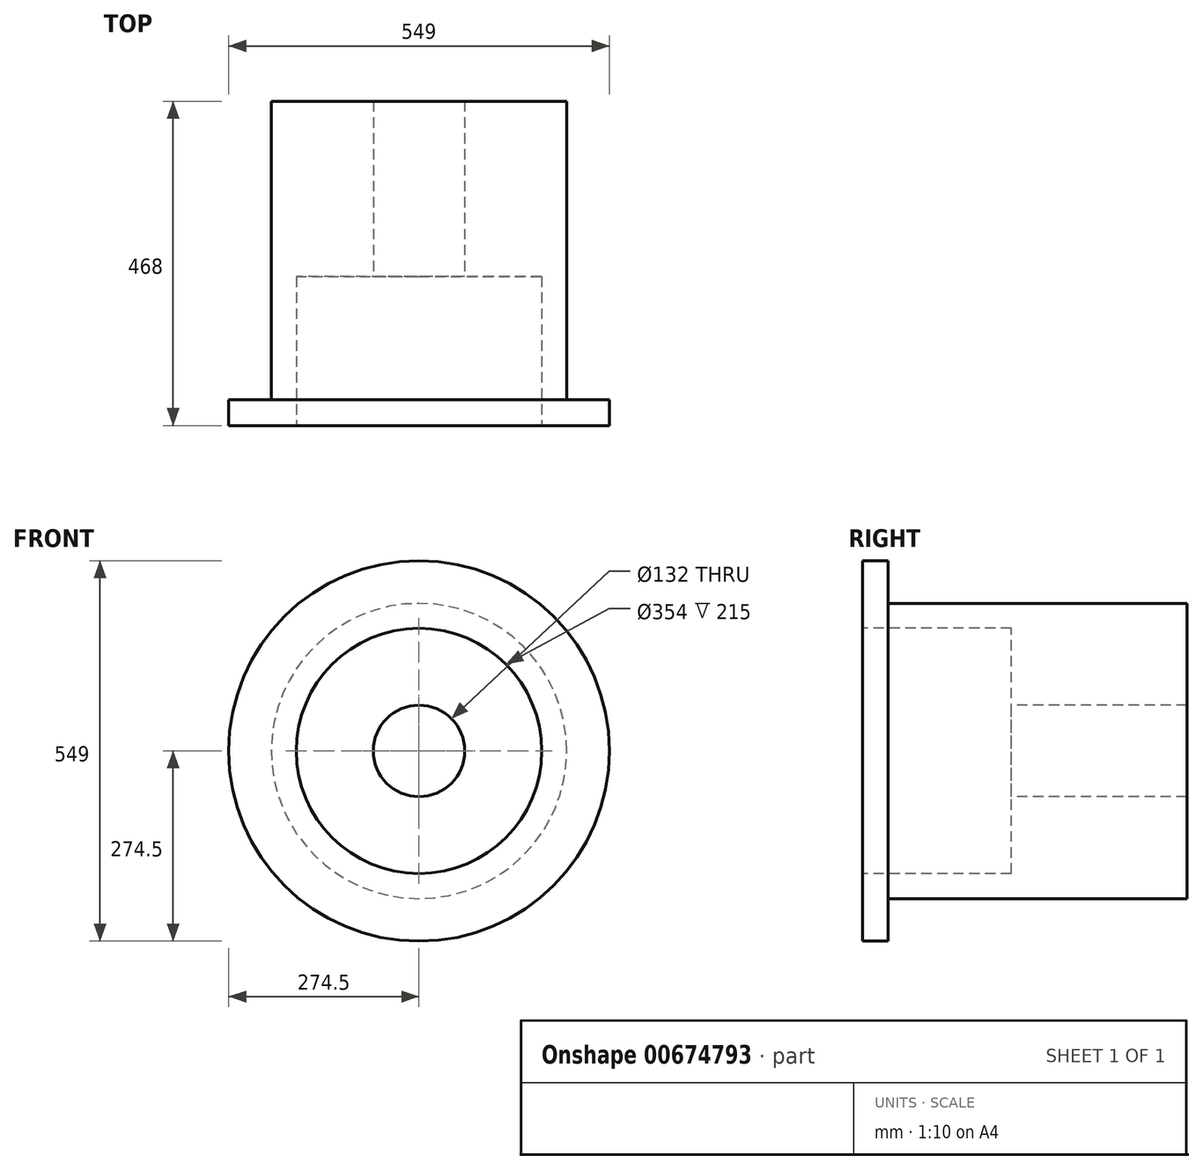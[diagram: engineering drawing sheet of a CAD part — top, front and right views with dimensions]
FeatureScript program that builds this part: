
annotation { "Feature Type Name" : "Feature", "Feature Type Description" : "" }
export const myFeature = defineFeature(function(context is Context, id is Id, definition is map)
    precondition{}
    {
        {
            var Q0;
            Q0=qCreatedBy(makeId("Front.planeOp"),FACE);
            var sketch = newSketch(context, id + "F0", { "sketchPlane" : qUnion([Q0])});
            skCircle(sketch, "E0", {"center": v(0, 0) * mm, "radius": 274.5 * mm});
            skSolve(sketch);
        }
        {
            var Q0;
            Q0=makeQuery(id+"F0.imprint","IMPRINT",FACE,{"disambiguationData":[TD([[makeQuery(id+"F0.imprint","IMPRINT",EDGE,{"derivedFrom":sQuery(id+"F0.wireOp",EDGE,"E0")}),1.0]])]});
            extrude(context, id + "F1", {"entities" : qUnion([Q0]), "depth" : 468 * mm, "offsetDistance" : 25 * mm});
        }
        {
            var Q0;
            Q0=makeQuery(id+"F1.opExtrude","CAP_FACE",FACE,{"disambiguationData":[OSD([sQuery(id+"F0.wireOp",EDGE,"E0")])],"isStart":false});
            var sketch = newSketch(context, id + "F2", { "sketchPlane" : qUnion([Q0])});
            skCircle(sketch, "E1", {"center": v(0, 0) * mm, "radius": 66 * mm});
            skSolve(sketch);
        }
        {
            var Q0;
            Q0=makeQuery(id+"F2.imprint","IMPRINT",FACE,{"disambiguationData":[TD([[makeQuery(id+"F2.imprint","IMPRINT",EDGE,{"derivedFrom":sQuery(id+"F2.wireOp",EDGE,"E1")}),1.0]])]});
            extrude(context, id + "F3", {"entities" : qUnion([Q0]), "operationType" : NewBodyOperationType.REMOVE, "oppositeDirection" : true, "depth" : 468 * mm, "offsetDistance" : 25 * mm});
        }
        {
            var Q0;
            Q0=makeQuery(id+"F1.opExtrude","CAP_FACE",FACE,{"disambiguationData":[OSD([sQuery(id+"F0.wireOp",EDGE,"E0")])],"isStart":false});
            var sketch = newSketch(context, id + "F4", { "sketchPlane" : qUnion([Q0])});
            skCircle(sketch, "E2", {"center": v(0, 0) * mm, "radius": 177 * mm});
            skSolve(sketch);
        }
        {
            var Q0;
            Q0=makeQuery(id+"F4.imprint","IMPRINT",FACE,{"disambiguationData":[TD([[makeQuery(id+"F4.imprint","IMPRINT",EDGE,{"derivedFrom":sQuery(id+"F4.wireOp",EDGE,"E2")}),1.0]])]});
            extrude(context, id + "F5", {"entities" : qUnion([Q0]), "operationType" : NewBodyOperationType.REMOVE, "oppositeDirection" : true, "depth" : 215 * mm, "offsetDistance" : 25 * mm});
        }
        {
            var Q0;
            Q0=makeQuery(id+"F1.opExtrude","CAP_FACE",FACE,{"disambiguationData":[OSD([sQuery(id+"F0.wireOp",EDGE,"E0")])],"isStart":true});
            var sketch = newSketch(context, id + "F6", { "sketchPlane" : qUnion([Q0])});
            skCircle(sketch, "E3", {"center": v(0, 0) * mm, "radius": 213 * mm});
            skSolve(sketch);
        }
        {
            var Q0;
            Q0=makeQuery(id+"F6.imprint","IMPRINT",FACE,{"disambiguationData":[TD([[makeQuery(id+"F6.imprint","IMPRINT",EDGE,{"derivedFrom":sQuery(id+"F6.wireOp",EDGE,"E3")}),-1.0]])]});
            extrude(context, id + "F7", {"entities" : qUnion([Q0]), "operationType" : NewBodyOperationType.REMOVE, "oppositeDirection" : true, "depth" : 431 * mm, "offsetDistance" : 25 * mm});
        }
    });
